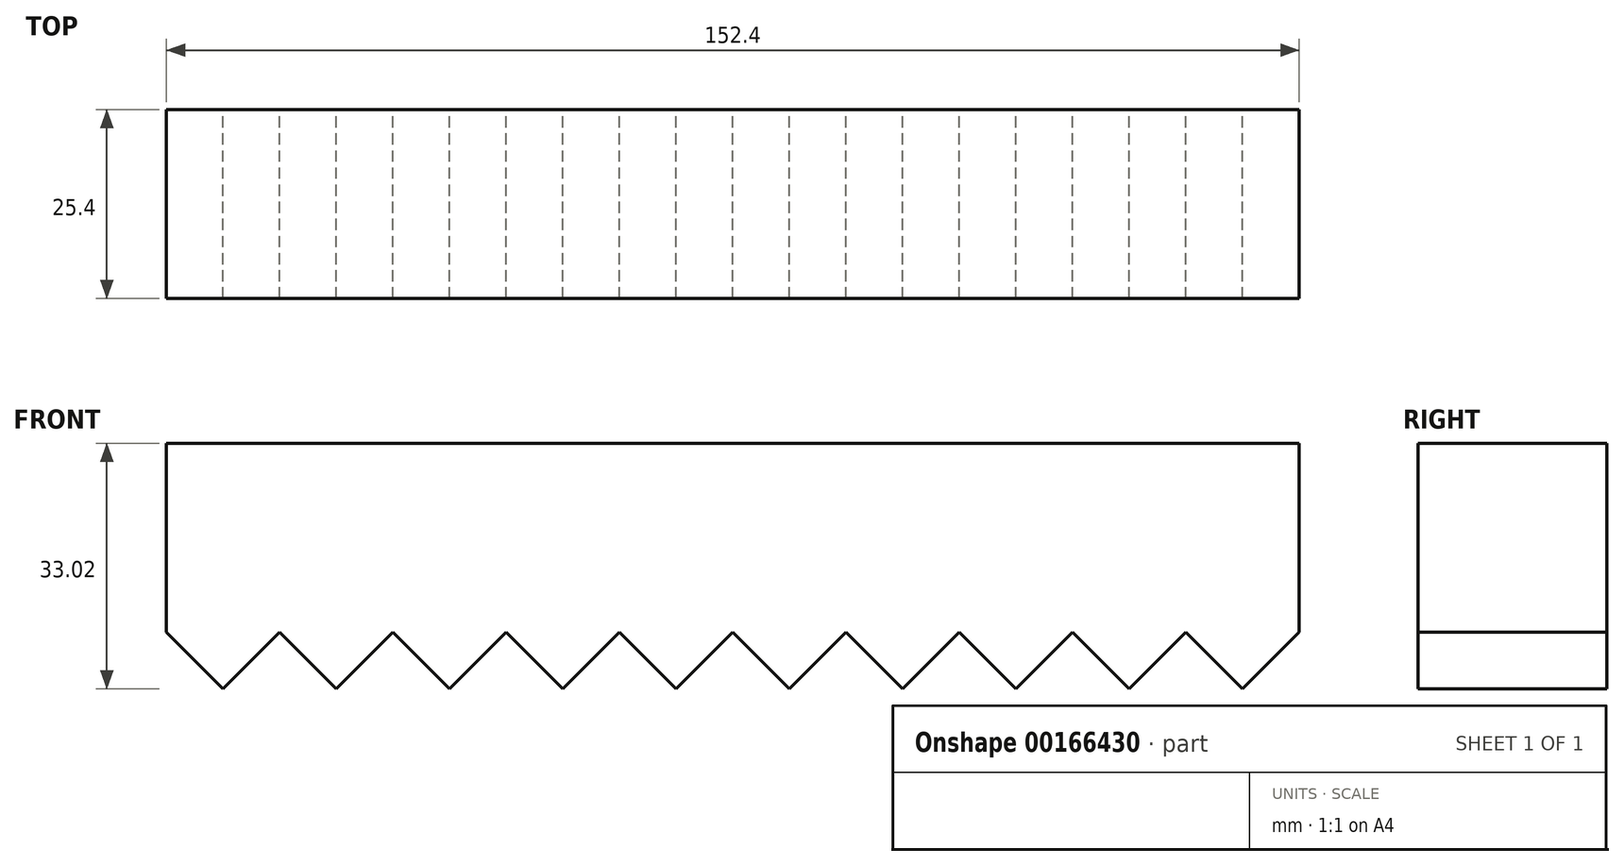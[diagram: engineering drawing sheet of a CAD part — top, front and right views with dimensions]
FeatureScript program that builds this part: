
annotation { "Feature Type Name" : "Feature", "Feature Type Description" : "" }
export const myFeature = defineFeature(function(context is Context, id is Id, definition is map)
    precondition{}
    {
        {
            var Q0;
            Q0=qCreatedBy(makeId("Front.planeOp"),FACE);
            var sketch = newSketch(context, id + "F0", { "sketchPlane" : qUnion([Q0])});
            skLineSegment(sketch, "E0.bottom", {"start": v(76.2, -12.7) * mm, "end": v(-76.2, -12.7) * mm});
            skLineSegment(sketch, "E0.top", {"start": v(76.2, 12.7) * mm, "end": v(-76.2, 12.7) * mm});
            skLineSegment(sketch, "E0.left", {"start": v(76.2, -12.7) * mm, "end": v(76.2, 12.7) * mm});
            skLineSegment(sketch, "E0.right", {"start": v(-76.2, -12.7) * mm, "end": v(-76.2, 12.7) * mm});
            skPoint(sketch, "E0.middle", {"position": v(0, 0) * mm});
            skLineSegment(sketch, "E1", {"start": v(-76.2, -12.7) * mm, "end": v(-60.96, -12.7) * mm});
            skLineSegment(sketch, "E2", {"start": v(-76.2, -12.7) * mm, "end": v(-68.58, -20.32) * mm});
            skLineSegment(sketch, "E3", {"start": v(-60.96, -12.7) * mm, "end": v(-68.58, -20.32) * mm});
            skLineSegment(sketch, "E4.1.0.0", {"start": v(-45.72, -12.7) * mm, "end": v(-53.34, -20.32) * mm});
            skLineSegment(sketch, "E4.1.0.1", {"start": v(-60.96, -12.7) * mm, "end": v(-53.34, -20.32) * mm});
            skLineSegment(sketch, "E4.2.0.0", {"start": v(-30.48, -12.7) * mm, "end": v(-38.1, -20.32) * mm});
            skLineSegment(sketch, "E4.2.0.1", {"start": v(-45.72, -12.7) * mm, "end": v(-38.1, -20.32) * mm});
            skLineSegment(sketch, "E4.3.0.0", {"start": v(-15.24, -12.7) * mm, "end": v(-22.86, -20.32) * mm});
            skLineSegment(sketch, "E4.3.0.1", {"start": v(-30.48, -12.7) * mm, "end": v(-22.86, -20.32) * mm});
            skLineSegment(sketch, "E4.4.0.0", {"start": v(0, -12.7) * mm, "end": v(-7.62, -20.32) * mm});
            skLineSegment(sketch, "E4.4.0.1", {"start": v(-15.24, -12.7) * mm, "end": v(-7.62, -20.32) * mm});
            skLineSegment(sketch, "E4.5.0.0", {"start": v(15.24, -12.7) * mm, "end": v(7.62, -20.32) * mm});
            skLineSegment(sketch, "E4.5.0.1", {"start": v(0, -12.7) * mm, "end": v(7.62, -20.32) * mm});
            skLineSegment(sketch, "E4.6.0.0", {"start": v(30.48, -12.7) * mm, "end": v(22.86, -20.32) * mm});
            skLineSegment(sketch, "E4.6.0.1", {"start": v(15.24, -12.7) * mm, "end": v(22.86, -20.32) * mm});
            skLineSegment(sketch, "E4.7.0.0", {"start": v(45.72, -12.7) * mm, "end": v(38.1, -20.32) * mm});
            skLineSegment(sketch, "E4.7.0.1", {"start": v(30.48, -12.7) * mm, "end": v(38.1, -20.32) * mm});
            skLineSegment(sketch, "E4.8.0.0", {"start": v(60.96, -12.7) * mm, "end": v(53.34, -20.32) * mm});
            skLineSegment(sketch, "E4.8.0.1", {"start": v(45.72, -12.7) * mm, "end": v(53.34, -20.32) * mm});
            skLineSegment(sketch, "E4.9.0.0", {"start": v(76.2, -12.7) * mm, "end": v(68.58, -20.32) * mm});
            skLineSegment(sketch, "E4.9.0.1", {"start": v(60.96, -12.7) * mm, "end": v(68.58, -20.32) * mm});
            skLineSegment(sketch, "E4.direction1", {"start": v(-68.58, -20.32) * mm, "end": v(-53.34, -20.32) * mm, "construction": true});
            skSolve(sketch);
        }
        {
            var Q0;
            Q0 = qSketchRegion(id + "F0", true);
            extrude(context, id + "F1", {"entities" : qUnion([Q0]), "depth" : 25.4 * mm});
        }
    });
